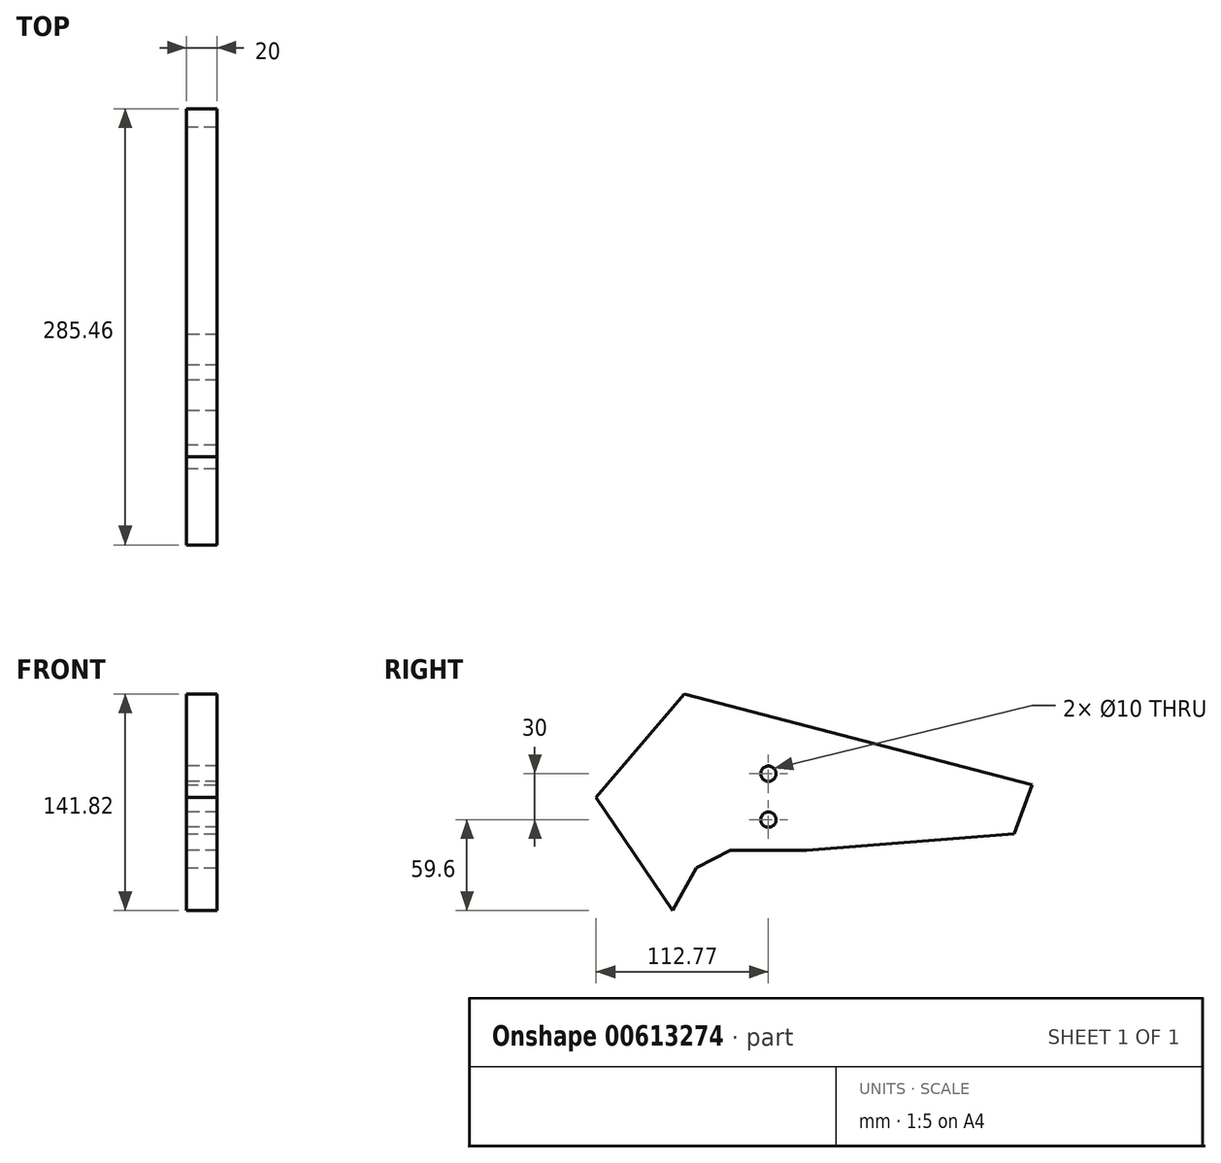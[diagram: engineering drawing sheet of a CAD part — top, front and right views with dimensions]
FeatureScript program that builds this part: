
annotation { "Feature Type Name" : "Feature", "Feature Type Description" : "" }
export const myFeature = defineFeature(function(context is Context, id is Id, definition is map)
    precondition{}
    {
        {
            var Q0;
            Q0=qCreatedBy(makeId("Right.planeOp"),FACE);
            var sketch = newSketch(context, id + "F0", { "sketchPlane" : qUnion([Q0])});
            skLineSegment(sketch, "E0.bottom", {"start": v(0, 0) * mm, "end": v(50, 0) * mm});
            skLineSegment(sketch, "E0.top", {"start": v(0, 70) * mm, "end": v(50, 70) * mm});
            skLineSegment(sketch, "E0.left", {"start": v(0, 0) * mm, "end": v(0, 70) * mm});
            skLineSegment(sketch, "E0.right", {"start": v(50, 0) * mm, "end": v(50, 70) * mm});
            skSolve(sketch);
        }
        {
            var Q0;
            Q0 = qSketchRegion(id + "F0", true);
            extrude(context, id + "F1", {"entities" : qUnion([Q0]), "depth" : 20 * mm, "offsetDistance" : 25 * mm});
        }
        {
            var Q0;
            Q0=makeQuery(id+"F1.opExtrude","CAP_FACE",FACE,{"disambiguationData":[OSD([sQuery(id+"F0.wireOp",EDGE,"E0.bottom"),sQuery(id+"F0.wireOp",EDGE,"E0.top"),sQuery(id+"F0.wireOp",EDGE,"E0.left"),sQuery(id+"F0.wireOp",EDGE,"E0.right")])],"isStart":false});
            var sketch = newSketch(context, id + "F2", { "sketchPlane" : qUnion([Q0])});
            skPoint(sketch, "E1", {"position": v(25, 50) * mm});
            skPoint(sketch, "E2", {"position": v(25, 20) * mm});
            skSolve(sketch);
        }
        {
            var Q0;
            Q0=sQuery(id+"F2.wireOp",VERTEX,"E2");
            var Q1;
            Q1=sQuery(id+"F2.wireOp",VERTEX,"E1");
            var Q2;
            Q2=makeQuery(id+"F1.opExtrude","SWEPT_BODY",BODY,{"disambiguationData":[OSD([sQuery(id+"F0.wireOp",EDGE,"E0.bottom"),sQuery(id+"F0.wireOp",EDGE,"E0.top"),sQuery(id+"F0.wireOp",EDGE,"E0.left"),sQuery(id+"F0.wireOp",EDGE,"E0.right")])]});
            hole(context, id + "F3", {"style" : HoleStyle.SIMPLE, "endStyle" : HoleEndStyle.BLIND, "holeDiameter" : 10 * mm, "majorDiameter" : 5 * mm, "holeDepth" : 100 * mm, "isTappedThrough" : true, "tappedDepth" : 12 * mm, "tapClearance" : 3, "locations" : qUnion([Q0, Q1]), "scope" : qUnion([Q2])});
        }
        {
            var Q0;
            Q0=makeQuery(id+"F1.opExtrude","CAP_FACE",FACE,{"disambiguationData":[OSD([sQuery(id+"F0.wireOp",EDGE,"E0.bottom"),sQuery(id+"F0.wireOp",EDGE,"E0.top"),sQuery(id+"F0.wireOp",EDGE,"E0.left"),sQuery(id+"F0.wireOp",EDGE,"E0.right")])],"isStart":false});
            var sketch = newSketch(context, id + "F4", { "sketchPlane" : qUnion([Q0])});
            skLineSegment(sketch, "E3", {"start": v(0, 0) * mm, "end": v(-22.04, -11.65) * mm});
            skLineSegment(sketch, "E4", {"start": v(-22.04, -11.65) * mm, "end": v(-37.82, -39.6) * mm});
            skLineSegment(sketch, "E5", {"start": v(-37.82, -39.6) * mm, "end": v(-87.77, 34.42) * mm});
            skLineSegment(sketch, "E6", {"start": v(-87.77, 34.42) * mm, "end": v(-30.06, 102.22) * mm});
            skLineSegment(sketch, "E7", {"start": v(-30.06, 102.22) * mm, "end": v(197.69, 42.7) * mm});
            skLineSegment(sketch, "E8", {"start": v(197.69, 42.7) * mm, "end": v(185.78, 10.6) * mm});
            skLineSegment(sketch, "E9", {"start": v(185.78, 10.6) * mm, "end": v(50, 0) * mm});
            skSolve(sketch);
        }
        {
            var Q0;
            Q0=makeQuery(id+"F4.imprint","IMPRINT",FACE,{"disambiguationData":[TD([[makeQuery(id+"F4.imprint","IMPRINT",EDGE,{"derivedFrom":sQuery(id+"F4.wireOp",EDGE,"E3")}),-1.0]])]});
            extrude(context, id + "F5", {"entities" : qUnion([Q0]), "operationType" : NewBodyOperationType.ADD, "oppositeDirection" : true, "depth" : 20 * mm, "offsetDistance" : 25 * mm});
        }
    });
